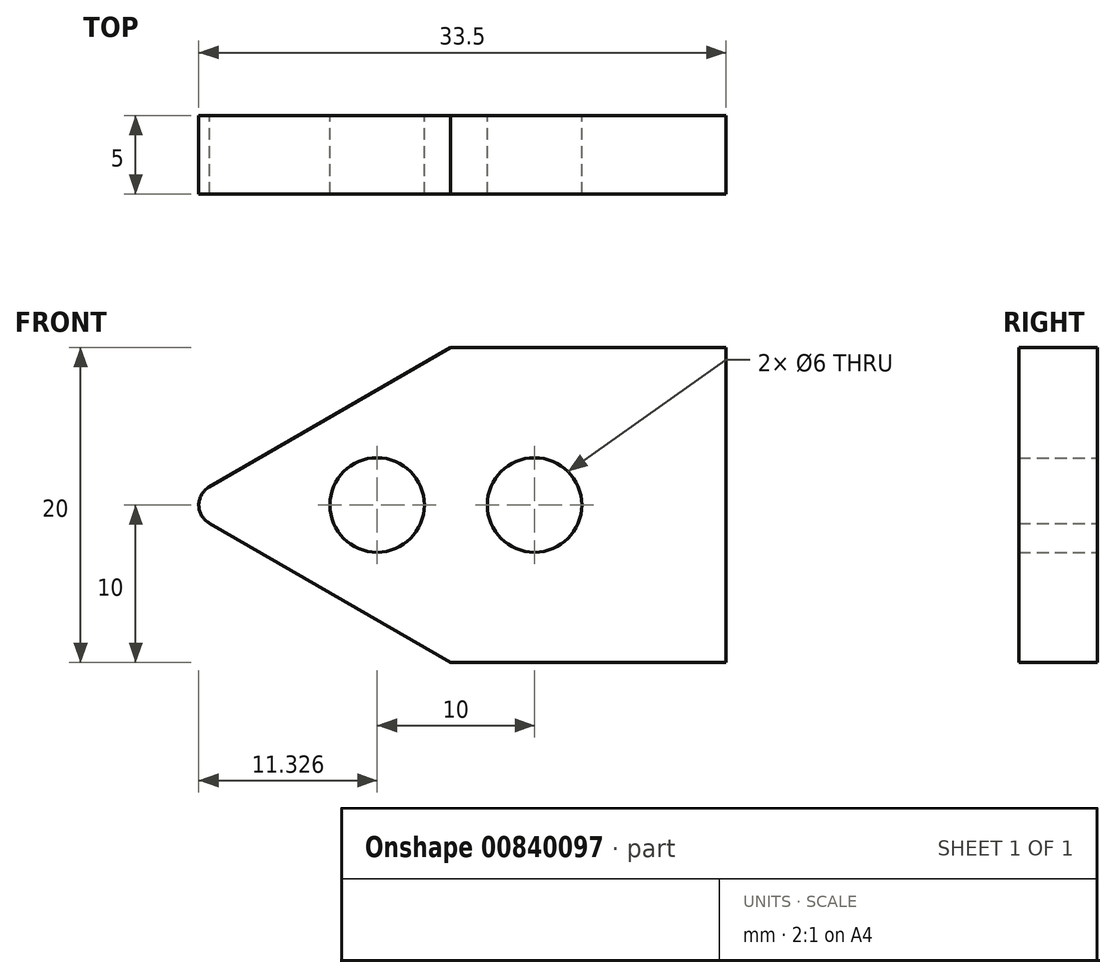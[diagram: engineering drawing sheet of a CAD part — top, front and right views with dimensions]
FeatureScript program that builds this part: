
annotation { "Feature Type Name" : "Feature", "Feature Type Description" : "" }
export const myFeature = defineFeature(function(context is Context, id is Id, definition is map)
    precondition{}
    {
        {
            var Q0;
            Q0=qCreatedBy(makeId("Front.planeOp"),FACE);
            var sketch = newSketch(context, id + "F0", { "sketchPlane" : qUnion([Q0])});
            skPoint(sketch, "E0", {"position": v(-31.24, 13.13) * mm});
            skCircle(sketch, "E1", {"center": v(-31.24, 13.13) * mm, "radius": 3 * mm});
            skLineSegment(sketch, "E2", {"start": v(-41.87, 11.96) * mm, "end": v(-41.94, 12) * mm});
            skArc(sketch, "E3", {"start": v(-41.9, 14.28) * mm, "mid": v(-42.57, 13.11) * mm, "end": v(-41.87, 11.96) * mm});
            skPoint(sketch, "E4", {"position": v(-21.24, 13.13) * mm});
            skCircle(sketch, "E5", {"center": v(-21.24, 13.13) * mm, "radius": 3 * mm});
            skLineSegment(sketch, "E6", {"start": v(-41.9, 14.28) * mm, "end": v(-26.57, 23.13) * mm});
            skLineSegment(sketch, "E7", {"start": v(-41.87, 11.96) * mm, "end": v(-26.57, 3.13) * mm});
            skPoint(sketch, "E8", {"position": v(-9.07, 23.13) * mm});
            skPoint(sketch, "E9", {"position": v(-9.07, 3.13) * mm});
            skLineSegment(sketch, "E10", {"start": v(-9.07, 23.13) * mm, "end": v(-26.57, 23.13) * mm});
            skLineSegment(sketch, "E11", {"start": v(-9.07, 3.13) * mm, "end": v(-26.57, 3.13) * mm});
            skLineSegment(sketch, "E12", {"start": v(-9.07, 23.13) * mm, "end": v(-9.07, 3.13) * mm});
            skSolve(sketch);
        }
        {
            var Q0;
            Q0 = qSketchRegion(id + "F0", true);
            extrude(context, id + "F1", {"entities" : qUnion([Q0]), "depth" : 5 * mm, "offsetDistance" : 25 * mm});
        }
    });
